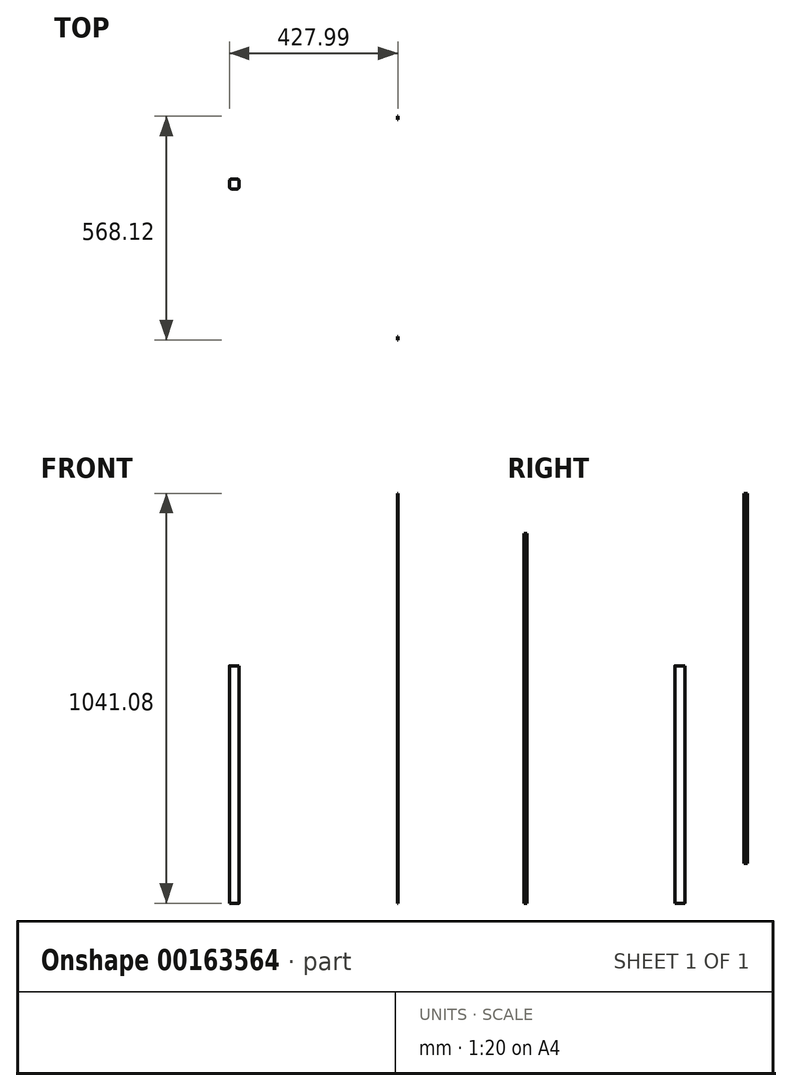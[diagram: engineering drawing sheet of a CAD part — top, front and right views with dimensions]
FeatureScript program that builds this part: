
annotation { "Feature Type Name" : "Feature", "Feature Type Description" : "" }
export const myFeature = defineFeature(function(context is Context, id is Id, definition is map)
    precondition{}
    {
        {
            var Q0;
            Q0=qCreatedBy(makeId("Top.planeOp"),FACE);
            var sketch = newSketch(context, id + "F0", { "sketchPlane" : qUnion([Q0])});
            skLineSegment(sketch, "E0.bottom", {"start": v(6.35, 12.7) * mm, "end": v(-6.35, 12.7) * mm});
            skLineSegment(sketch, "E0.top", {"start": v(6.35, -12.7) * mm, "end": v(-6.35, -12.7) * mm});
            skLineSegment(sketch, "E0.left", {"start": v(12.7, 6.35) * mm, "end": v(12.7, -6.35) * mm});
            skLineSegment(sketch, "E0.right", {"start": v(-12.7, 6.35) * mm, "end": v(-12.7, -6.35) * mm});
            skPoint(sketch, "E0.middle", {"position": v(0, 0) * mm});
            skPoint(sketch, "E1.visualSharp", {"position": v(-12.7, 12.7) * mm});
            skArc(sketch, "E1.filletArc", {"start": v(-6.35, 12.7) * mm, "mid": v(-10.84, 10.84) * mm, "end": v(-12.7, 6.35) * mm});
            skPoint(sketch, "E2.visualSharp", {"position": v(-12.7, -12.7) * mm});
            skArc(sketch, "E2.filletArc", {"start": v(-12.7, -6.35) * mm, "mid": v(-10.84, -10.84) * mm, "end": v(-6.35, -12.7) * mm});
            skPoint(sketch, "E3.visualSharp", {"position": v(12.7, -12.7) * mm});
            skArc(sketch, "E3.filletArc", {"start": v(6.35, -12.7) * mm, "mid": v(10.84, -10.84) * mm, "end": v(12.7, -6.35) * mm});
            skPoint(sketch, "E4.visualSharp", {"position": v(12.7, 12.7) * mm});
            skArc(sketch, "E4.filletArc", {"start": v(12.7, 6.35) * mm, "mid": v(10.84, 10.84) * mm, "end": v(6.35, 12.7) * mm});
            skSolve(sketch);
        }
        {
            var Q0;
            Q0=qSketchRegion(id+"F0",true);
            extrude(context, id + "F1", {"entities" : qUnion([Q0]), "depth" : 603.25 * mm});
        }
        {
            var Q0;
            Q0=qCreatedBy(makeId("Right.planeOp"),FACE);
            var sketch = newSketch(context, id + "F2", { "sketchPlane" : qUnion([Q0])});
            skLineSegment(sketch, "E5.bottom", {"start": v(-396.35, 939.8) * mm, "end": v(-387.88, 939.8) * mm});
            skLineSegment(sketch, "E5.top", {"start": v(-396.35, 0) * mm, "end": v(-387.88, 0) * mm});
            skLineSegment(sketch, "E5.left", {"start": v(-396.35, 939.8) * mm, "end": v(-396.35, 0) * mm});
            skLineSegment(sketch, "E5.right", {"start": v(-387.88, 939.8) * mm, "end": v(-387.88, 0) * mm});
            skSolve(sketch);
        }
        {
            var Q0;
            Q0=qSketchRegion(id+"F2",true);
            extrude(context, id + "F3", {"entities" : qUnion([Q0]), "depth" : 1.27 * mm});
        }
        {
            var Q0;
            Q0=qCreatedBy(makeId("Right.planeOp"),FACE);
            var sketch = newSketch(context, id + "F4", { "sketchPlane" : qUnion([Q0])});
            skLineSegment(sketch, "E6.bottom", {"start": v(163.3, 1041.08) * mm, "end": v(171.77, 1041.08) * mm});
            skLineSegment(sketch, "E6.top", {"start": v(163.3, 101.28) * mm, "end": v(171.77, 101.28) * mm});
            skLineSegment(sketch, "E6.left", {"start": v(163.3, 1041.08) * mm, "end": v(163.3, 101.28) * mm});
            skLineSegment(sketch, "E6.right", {"start": v(171.77, 1041.08) * mm, "end": v(171.77, 101.28) * mm});
            skSolve(sketch);
        }
        {
            var Q0;
            Q0=qSketchRegion(id+"F4",true);
            extrude(context, id + "F5", {"entities" : qUnion([Q0]), "depth" : 1.27 * mm});
        }
        {
            var Q0;
            Q0=makeQuery(id+"F5.opExtrude","SWEPT_BODY",BODY,{"disambiguationData":[OSD([sQuery(id+"F4.wireOp",EDGE,"E6.bottom"),sQuery(id+"F4.wireOp",EDGE,"E6.top"),sQuery(id+"F4.wireOp",EDGE,"E6.left"),sQuery(id+"F4.wireOp",EDGE,"E6.right")])]});
            var Q1;
            Q1=makeQuery(id+"F3.opExtrude","SWEPT_BODY",BODY,{"disambiguationData":[OSD([sQuery(id+"F2.wireOp",EDGE,"E5.bottom"),sQuery(id+"F2.wireOp",EDGE,"E5.top"),sQuery(id+"F2.wireOp",EDGE,"E5.left"),sQuery(id+"F2.wireOp",EDGE,"E5.right")])]});
            transform(context, id + "F6", {"entities" : qUnion([Q0, Q1]), "transformType" : TransformType.TRANSLATION_3D, "dx" : 414.02 * mm, "dy" : 0 * mm, "dz" : 0 * mm, "makeCopy" : false});
        }
    });
